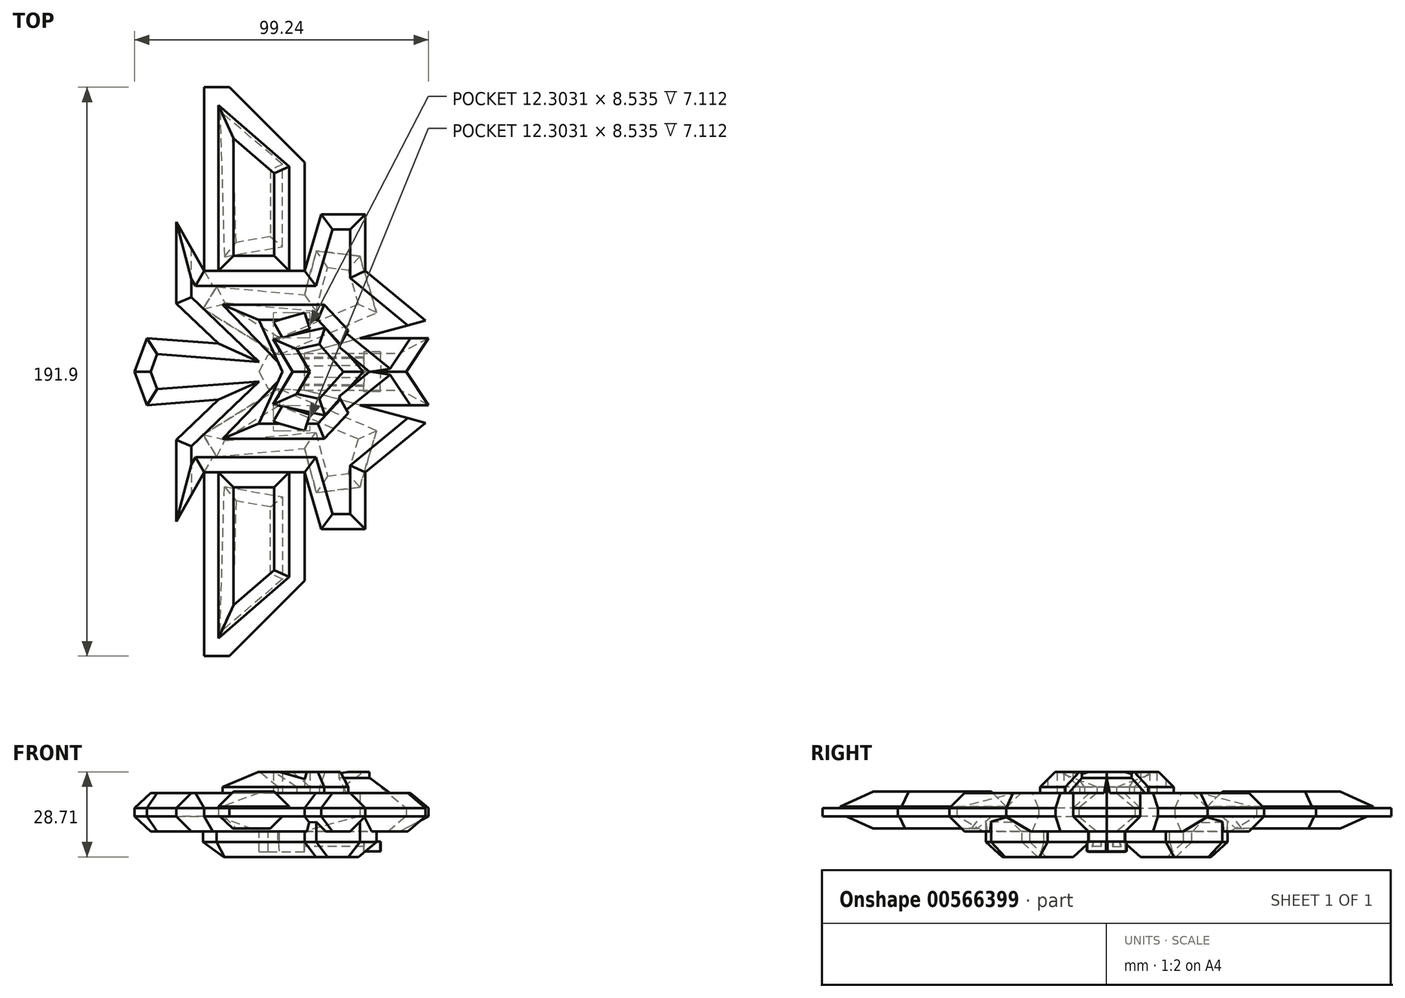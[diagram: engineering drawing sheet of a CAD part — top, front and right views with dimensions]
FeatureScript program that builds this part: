
annotation { "Feature Type Name" : "Feature", "Feature Type Description" : "" }
export const myFeature = defineFeature(function(context is Context, id is Id, definition is map)
    precondition{}
    {
        {
            var Q0;
            Q0=qCreatedBy(makeId("Top.planeOp"),FACE);
            var sketch = newSketch(context, id + "F0", { "sketchPlane" : qUnion([Q0])});
            skLineSegment(sketch, "E0", {"start": v(-57.4, 0) * mm, "end": v(-53.2, 11.26) * mm});
            skLineSegment(sketch, "E1", {"start": v(-53.2, 11.26) * mm, "end": v(-29.1, 9.47) * mm});
            skLineSegment(sketch, "E2", {"start": v(-29.1, 9.47) * mm, "end": v(-43.24, 23.02) * mm});
            skLineSegment(sketch, "E3", {"start": v(-43.24, 23.02) * mm, "end": v(-43.24, 50.52) * mm});
            skLineSegment(sketch, "E4", {"start": v(-43.24, 50.52) * mm, "end": v(-33.88, 33.98) * mm});
            skLineSegment(sketch, "E5", {"start": v(-33.88, 33.98) * mm, "end": v(0, 33.98) * mm});
            skLineSegment(sketch, "E6", {"start": v(0, 33.98) * mm, "end": v(5.58, 53.1) * mm});
            skLineSegment(sketch, "E7", {"start": v(5.58, 53.1) * mm, "end": v(20.53, 53.1) * mm});
            skLineSegment(sketch, "E8", {"start": v(20.53, 53.1) * mm, "end": v(20.53, 33.98) * mm});
            skLineSegment(sketch, "E9", {"start": v(20.53, 33.98) * mm, "end": v(40.85, 17.24) * mm});
            skLineSegment(sketch, "E10", {"start": v(40.85, 17.24) * mm, "end": v(18.73, 11.26) * mm});
            skLineSegment(sketch, "E11", {"start": v(18.73, 11.26) * mm, "end": v(41.85, 11.26) * mm});
            skLineSegment(sketch, "E12", {"start": v(41.85, 11.26) * mm, "end": v(34.28, 0) * mm});
            skLineSegment(sketch, "E13", {"start": v(34.28, 0) * mm, "end": v(-57.4, 0) * mm});
            skSolve(sketch);
        }
        {
            var Q0;
            Q0 = qSketchRegion(id + "F0", true);
            extrude(context, id + "F1", {"entities" : qUnion([Q0]), "depth" : 12.95 * mm, "offsetDistance" : 25.4 * mm});
        }
        {
            var Q0;
            Q0=makeQuery(id+"F1.opExtrude","CAP_EDGE",EDGE,{"disambiguationData":[OSD([sQuery(id+"F0.wireOp",EDGE,"E0")])],"isStart":false});
            var Q1;
            Q1=makeQuery(id+"F1.opExtrude","CAP_EDGE",EDGE,{"disambiguationData":[OSD([sQuery(id+"F0.wireOp",EDGE,"E2")])],"isStart":false});
            var Q2;
            Q2=makeQuery(id+"F1.opExtrude","CAP_EDGE",EDGE,{"disambiguationData":[OSD([sQuery(id+"F0.wireOp",EDGE,"E3")])],"isStart":false});
            var Q3;
            Q3=makeQuery(id+"F1.opExtrude","CAP_EDGE",EDGE,{"disambiguationData":[OSD([sQuery(id+"F0.wireOp",EDGE,"E1")])],"isStart":false});
            var Q4;
            Q4=makeQuery(id+"F1.opExtrude","CAP_EDGE",EDGE,{"disambiguationData":[OSD([sQuery(id+"F0.wireOp",EDGE,"E4")])],"isStart":false});
            var Q5;
            Q5=makeQuery(id+"F1.opExtrude","CAP_EDGE",EDGE,{"disambiguationData":[OSD([sQuery(id+"F0.wireOp",EDGE,"E5")])],"isStart":false});
            var Q6;
            Q6=makeQuery(id+"F1.opExtrude","CAP_EDGE",EDGE,{"disambiguationData":[OSD([sQuery(id+"F0.wireOp",EDGE,"E6")])],"isStart":false});
            var Q7;
            Q7=makeQuery(id+"F1.opExtrude","CAP_EDGE",EDGE,{"disambiguationData":[OSD([sQuery(id+"F0.wireOp",EDGE,"E8")])],"isStart":false});
            var Q8;
            Q8=makeQuery(id+"F1.opExtrude","CAP_EDGE",EDGE,{"disambiguationData":[OSD([sQuery(id+"F0.wireOp",EDGE,"E7")])],"isStart":false});
            var Q9;
            Q9=makeQuery(id+"F1.opExtrude","CAP_EDGE",EDGE,{"disambiguationData":[OSD([sQuery(id+"F0.wireOp",EDGE,"E9")])],"isStart":false});
            var Q10;
            Q10=makeQuery(id+"F1.opExtrude","CAP_EDGE",EDGE,{"disambiguationData":[OSD([sQuery(id+"F0.wireOp",EDGE,"E11")])],"isStart":true});
            var Q11;
            Q11=makeQuery(id+"F1.opExtrude","CAP_EDGE",EDGE,{"disambiguationData":[OSD([sQuery(id+"F0.wireOp",EDGE,"E12")])],"isStart":false});
            chamfer(context, id + "F2", {"entities" : qUnion([Q0, Q1, Q2, Q3, Q4, Q5, Q6, Q7, Q8, Q9, Q10, Q11]), "width" : 5.08 * mm, "tangentPropagation" : true});
        }
        {
            var Q0;
            Q0=makeQuery(id+"F1.opExtrude","CAP_FACE",FACE,{"disambiguationData":[OSD([sQuery(id+"F0.wireOp",EDGE,"E0"),sQuery(id+"F0.wireOp",EDGE,"E1"),sQuery(id+"F0.wireOp",EDGE,"E2"),sQuery(id+"F0.wireOp",EDGE,"E3"),sQuery(id+"F0.wireOp",EDGE,"E4"),sQuery(id+"F0.wireOp",EDGE,"E5"),sQuery(id+"F0.wireOp",EDGE,"E6"),sQuery(id+"F0.wireOp",EDGE,"E7"),sQuery(id+"F0.wireOp",EDGE,"E8"),sQuery(id+"F0.wireOp",EDGE,"E9"),sQuery(id+"F0.wireOp",EDGE,"E10"),sQuery(id+"F0.wireOp",EDGE,"E11"),sQuery(id+"F0.wireOp",EDGE,"E12"),sQuery(id+"F0.wireOp",EDGE,"E13")])],"isStart":false});
            var sketch = newSketch(context, id + "F3", { "sketchPlane" : qUnion([Q0])});
            skLineSegment(sketch, "E14", {"start": v(-8.99, 3.35) * mm, "end": v(-27.62, 22.55) * mm});
            skLineSegment(sketch, "E15", {"start": v(-27.62, 22.55) * mm, "end": v(6.61, 22.55) * mm});
            skLineSegment(sketch, "E16", {"start": v(6.61, 22.55) * mm, "end": v(14.75, 13.94) * mm});
            skLineSegment(sketch, "E17", {"start": v(14.75, 13.94) * mm, "end": v(11.64, 8.39) * mm});
            skLineSegment(sketch, "E18", {"start": v(11.64, 8.39) * mm, "end": v(21.94, 0) * mm});
            skLineSegment(sketch, "E19", {"start": v(21.94, 0) * mm, "end": v(13.07, 0) * mm});
            skLineSegment(sketch, "E20", {"start": v(13.07, 0) * mm, "end": v(5.04, 9.2) * mm});
            skLineSegment(sketch, "E21", {"start": v(5.04, 9.2) * mm, "end": v(-2.64, 7.56) * mm});
            skLineSegment(sketch, "E22", {"start": v(-2.64, 7.56) * mm, "end": v(1.8, 0) * mm});
            skLineSegment(sketch, "E23", {"start": v(1.8, 0) * mm, "end": v(-7.47, 0) * mm});
            skLineSegment(sketch, "E24", {"start": v(-7.47, 0) * mm, "end": v(-8.99, 3.35) * mm});
            skLineSegment(sketch, "E25", {"start": v(-10.5, 16.83) * mm, "end": v(-7.47, 11.45) * mm});
            skPoint(sketch, "E25.startSnap0", {"position": v(-10.5, 22.55) * mm});
            skLineSegment(sketch, "E26", {"start": v(-7.47, 11.45) * mm, "end": v(1.8, 14.47) * mm});
            skLineSegment(sketch, "E27", {"start": v(1.8, 14.47) * mm, "end": v(0, 19.98) * mm});
            skLineSegment(sketch, "E28", {"start": v(0, 19.98) * mm, "end": v(-10.5, 16.83) * mm});
            skSolve(sketch);
        }
        {
            var Q0;
            Q0 = qSketchRegion(id + "F3", true);
            extrude(context, id + "F4", {"entities" : qUnion([Q0]), "operationType" : NewBodyOperationType.ADD, "depth" : 7.11 * mm, "offsetDistance" : 25.4 * mm});
        }
        {
            var Q0;
            Q0=makeQuery(id+"F4.opExtrude","CAP_EDGE",EDGE,{"disambiguationData":[OSD([sQuery(id+"F3.wireOp",EDGE,"E15")])],"isStart":false});
            var Q1;
            Q1=makeQuery(id+"F4.opExtrude","CAP_EDGE",EDGE,{"disambiguationData":[OSD([sQuery(id+"F3.wireOp",EDGE,"E16")])],"isStart":false});
            var Q2;
            Q2=makeQuery(id+"F4.opExtrude","CAP_EDGE",EDGE,{"disambiguationData":[OSD([sQuery(id+"F3.wireOp",EDGE,"E18")])],"isStart":true});
            var Q3;
            Q3=makeQuery(id+"F4.opExtrude","CAP_EDGE",EDGE,{"disambiguationData":[OSD([sQuery(id+"F3.wireOp",EDGE,"E14")])],"isStart":false});
            var Q4;
            Q4=makeQuery(id+"F4.opExtrude","CAP_EDGE",EDGE,{"disambiguationData":[OSD([sQuery(id+"F3.wireOp",EDGE,"E21")])],"isStart":false});
            var Q5;
            Q5=makeQuery(id+"F4.opExtrude","CAP_EDGE",EDGE,{"disambiguationData":[OSD([sQuery(id+"F3.wireOp",EDGE,"E20")])],"isStart":false});
            var Q6;
            Q6=makeQuery(id+"F4.opExtrude","CAP_EDGE",EDGE,{"disambiguationData":[OSD([sQuery(id+"F3.wireOp",EDGE,"E22")])],"isStart":false});
            chamfer(context, id + "F5", {"entities" : qUnion([Q0, Q1, Q2, Q3, Q4, Q5, Q6]), "width" : 5.08 * mm, "tangentPropagation" : true});
        }
        {
            var Q0;
            Q0=makeQuery(id+"F1.opExtrude","CAP_FACE",FACE,{"disambiguationData":[OSD([sQuery(id+"F0.wireOp",EDGE,"E0"),sQuery(id+"F0.wireOp",EDGE,"E1"),sQuery(id+"F0.wireOp",EDGE,"E2"),sQuery(id+"F0.wireOp",EDGE,"E3"),sQuery(id+"F0.wireOp",EDGE,"E4"),sQuery(id+"F0.wireOp",EDGE,"E5"),sQuery(id+"F0.wireOp",EDGE,"E6"),sQuery(id+"F0.wireOp",EDGE,"E7"),sQuery(id+"F0.wireOp",EDGE,"E8"),sQuery(id+"F0.wireOp",EDGE,"E9"),sQuery(id+"F0.wireOp",EDGE,"E10"),sQuery(id+"F0.wireOp",EDGE,"E11"),sQuery(id+"F0.wireOp",EDGE,"E12"),sQuery(id+"F0.wireOp",EDGE,"E13")])],"isStart":true});
            var sketch = newSketch(context, id + "F6", { "sketchPlane" : qUnion([Q0])});
            skLineSegment(sketch, "E29", {"start": v(24.3, -19.9) * mm, "end": v(-8.87, -5.66) * mm});
            skLineSegment(sketch, "E30", {"start": v(-8.87, -5.66) * mm, "end": v(-34.2, -21.2) * mm});
            skLineSegment(sketch, "E31", {"start": v(-34.2, -21.2) * mm, "end": v(-29.64, -28.65) * mm});
            skLineSegment(sketch, "E32", {"start": v(-29.64, -28.65) * mm, "end": v(0, -25.9) * mm});
            skLineSegment(sketch, "E33", {"start": v(0, -25.9) * mm, "end": v(3.99, -40.8) * mm});
            skLineSegment(sketch, "E34", {"start": v(3.99, -40.8) * mm, "end": v(18.64, -38.95) * mm});
            skLineSegment(sketch, "E35", {"start": v(18.64, -38.95) * mm, "end": v(24.3, -19.9) * mm});
            skSolve(sketch);
        }
        {
            var Q0;
            Q0 = qSketchRegion(id + "F6", true);
            extrude(context, id + "F7", {"entities" : qUnion([Q0]), "operationType" : NewBodyOperationType.ADD, "depth" : 8.64 * mm, "offsetDistance" : 25.4 * mm});
        }
        {
            var Q0;
            Q0=makeQuery(id+"F7.opExtrude","CAP_EDGE",EDGE,{"disambiguationData":[OSD([sQuery(id+"F6.wireOp",EDGE,"E35")])],"isStart":false});
            var Q1;
            Q1=makeQuery(id+"F7.opExtrude","CAP_EDGE",EDGE,{"disambiguationData":[OSD([sQuery(id+"F6.wireOp",EDGE,"E33")])],"isStart":false});
            var Q2;
            Q2=makeQuery(id+"F7.opExtrude","CAP_EDGE",EDGE,{"disambiguationData":[OSD([sQuery(id+"F6.wireOp",EDGE,"E29")])],"isStart":false});
            var Q3;
            Q3=makeQuery(id+"F7.opExtrude","CAP_EDGE",EDGE,{"disambiguationData":[OSD([sQuery(id+"F6.wireOp",EDGE,"E30")])],"isStart":false});
            var Q4;
            Q4=makeQuery(id+"F7.opExtrude","CAP_EDGE",EDGE,{"disambiguationData":[OSD([sQuery(id+"F6.wireOp",EDGE,"E31")])],"isStart":false});
            var Q5;
            Q5=makeQuery(id+"F7.opExtrude","CAP_EDGE",EDGE,{"disambiguationData":[OSD([sQuery(id+"F6.wireOp",EDGE,"E32")])],"isStart":false});
            var Q6;
            Q6=makeQuery(id+"F7.opExtrude","CAP_EDGE",EDGE,{"disambiguationData":[OSD([sQuery(id+"F6.wireOp",EDGE,"E34")])],"isStart":false});
            chamfer(context, id + "F8", {"entities" : qUnion([Q0, Q1, Q2, Q3, Q4, Q5, Q6]), "width" : 5.08 * mm, "tangentPropagation" : true});
        }
        {
            var Q0;
            Q0=makeQuery(id+"F1.opExtrude","CAP_EDGE",EDGE,{"disambiguationData":[OSD([sQuery(id+"F0.wireOp",EDGE,"E0")])],"isStart":true});
            var Q1;
            Q1=makeQuery(id+"F1.opExtrude","CAP_EDGE",EDGE,{"disambiguationData":[OSD([sQuery(id+"F0.wireOp",EDGE,"E1")])],"isStart":true});
            var Q2;
            Q2=makeQuery(id+"F1.opExtrude","CAP_EDGE",EDGE,{"disambiguationData":[OSD([sQuery(id+"F0.wireOp",EDGE,"E2")])],"isStart":true});
            var Q3;
            Q3=makeQuery(id+"F1.opExtrude","CAP_EDGE",EDGE,{"disambiguationData":[OSD([sQuery(id+"F0.wireOp",EDGE,"E3")])],"isStart":true});
            var Q4;
            Q4=makeQuery(id+"F1.opExtrude","CAP_EDGE",EDGE,{"disambiguationData":[OSD([sQuery(id+"F0.wireOp",EDGE,"E5")])],"isStart":true});
            var Q5;
            Q5=makeQuery(id+"F1.opExtrude","CAP_EDGE",EDGE,{"disambiguationData":[OSD([sQuery(id+"F0.wireOp",EDGE,"E6")])],"isStart":true});
            var Q6;
            Q6=makeQuery(id+"F1.opExtrude","CAP_EDGE",EDGE,{"disambiguationData":[OSD([sQuery(id+"F0.wireOp",EDGE,"E7")])],"isStart":true});
            var Q7;
            Q7=makeQuery(id+"F1.opExtrude","CAP_EDGE",EDGE,{"disambiguationData":[OSD([sQuery(id+"F0.wireOp",EDGE,"E8")])],"isStart":true});
            var Q8;
            Q8=makeQuery(id+"F1.opExtrude","CAP_EDGE",EDGE,{"disambiguationData":[OSD([sQuery(id+"F0.wireOp",EDGE,"E9")])],"isStart":true});
            var Q9;
            Q9=makeQuery(id+"F1.opExtrude","CAP_EDGE",EDGE,{"disambiguationData":[OSD([sQuery(id+"F0.wireOp",EDGE,"E12")])],"isStart":true});
            chamfer(context, id + "F9", {"entities" : qUnion([Q0, Q1, Q2, Q3, Q4, Q5, Q6, Q7, Q8, Q9]), "width" : 5.08 * mm, "tangentPropagation" : true});
        }
        {
            var Q0;
            Q0=makeQuery(id+"F1.opExtrude","SWEPT_FACE",FACE,{"disambiguationData":[OSD([sQuery(id+"F0.wireOp",EDGE,"E5")])]});
            var sketch = newSketch(context, id + "F10", { "sketchPlane" : qUnion([Q0])});
            skLineSegment(sketch, "E36", {"start": v(33.88, 7.87) * mm, "end": v(33.88, 5.08) * mm});
            skLineSegment(sketch, "E37", {"start": v(33.88, 5.08) * mm, "end": v(0, 5.08) * mm});
            skLineSegment(sketch, "E38", {"start": v(0, 5.08) * mm, "end": v(0, 7.87) * mm});
            skLineSegment(sketch, "E39", {"start": v(0, 7.87) * mm, "end": v(33.88, 7.87) * mm});
            skSolve(sketch);
        }
        {
            var Q0;
            Q0 = qSketchRegion(id + "F10", true);
            extrude(context, id + "F11", {"entities" : qUnion([Q0]), "operationType" : NewBodyOperationType.ADD, "depth" : 61.98 * mm, "offsetDistance" : 25.4 * mm});
        }
        {
            var Q0;
            Q0=makeQuery(id+"F11.opExtrude","CAP_EDGE",EDGE,{"disambiguationData":[OSD([sQuery(id+"F10.wireOp",EDGE,"E38")])],"isStart":false});
            chamfer(context, id + "F12", {"entities" : qUnion([Q0]), "width" : 25.4 * mm, "tangentPropagation" : true});
        }
        {
            var Q0;
            Q0=makeQuery(id+"F11.opExtrude","SWEPT_FACE",FACE,{"disambiguationData":[OSD([sQuery(id+"F10.wireOp",EDGE,"E39")])]});
            var sketch = newSketch(context, id + "F13", { "sketchPlane" : qUnion([Q0])});
            skLineSegment(sketch, "E40", {"start": v(-29.04, 33.98) * mm, "end": v(-29.04, 89.9) * mm});
            skLineSegment(sketch, "E41", {"start": v(-29.04, 89.9) * mm, "end": v(-5.18, 69.2) * mm});
            skLineSegment(sketch, "E42", {"start": v(-5.18, 69.2) * mm, "end": v(-5.18, 33.98) * mm});
            skLineSegment(sketch, "E43", {"start": v(-5.18, 33.98) * mm, "end": v(-29.04, 33.98) * mm});
            skSolve(sketch);
        }
        {
            var Q0;
            Q0 = qSketchRegion(id + "F13", true);
            extrude(context, id + "F14", {"entities" : qUnion([Q0]), "operationType" : NewBodyOperationType.ADD, "depth" : 5.6 * mm, "offsetDistance" : 25.4 * mm});
        }
        {
            var Q0;
            Q0=makeQuery(id+"F14.opExtrude","CAP_EDGE",EDGE,{"disambiguationData":[OSD([sQuery(id+"F13.wireOp",EDGE,"E40")])],"isStart":false});
            var Q1;
            Q1=makeQuery(id+"F14.opExtrude","CAP_EDGE",EDGE,{"disambiguationData":[OSD([sQuery(id+"F13.wireOp",EDGE,"E41")])],"isStart":false});
            var Q2;
            Q2=makeQuery(id+"F14.opExtrude","CAP_EDGE",EDGE,{"disambiguationData":[OSD([sQuery(id+"F13.wireOp",EDGE,"E42")])],"isStart":false});
            var Q3;
            Q3=makeQuery(id+"F14.opExtrude","CAP_EDGE",EDGE,{"disambiguationData":[OSD([sQuery(id+"F13.wireOp",EDGE,"E43")])],"isStart":false});
            chamfer(context, id + "F15", {"entities" : qUnion([Q0, Q1, Q2, Q3]), "width" : 5.08 * mm, "tangentPropagation" : true});
        }
        {
            var Q0;
            Q0=makeQuery(id+"F11.opExtrude","SWEPT_FACE",FACE,{"disambiguationData":[OSD([sQuery(id+"F10.wireOp",EDGE,"E37")])]});
            var sketch = newSketch(context, id + "F16", { "sketchPlane" : qUnion([Q0])});
            skLineSegment(sketch, "E44", {"start": v(-29.59, -90.15) * mm, "end": v(-6.43, -70.44) * mm});
            skLineSegment(sketch, "E45", {"start": v(-6.43, -70.44) * mm, "end": v(-6.43, -41.3) * mm});
            skLineSegment(sketch, "E46", {"start": v(-6.43, -41.3) * mm, "end": v(-28.05, -37.59) * mm});
            skLineSegment(sketch, "E47", {"start": v(-28.05, -37.59) * mm, "end": v(-29.59, -90.15) * mm});
            skSolve(sketch);
        }
        {
            var Q0;
            Q0 = qSketchRegion(id + "F16", true);
            extrude(context, id + "F17", {"entities" : qUnion([Q0]), "operationType" : NewBodyOperationType.ADD, "depth" : 4.06 * mm, "offsetDistance" : 25.4 * mm});
        }
        {
            var Q0;
            Q0=makeQuery(id+"F17.opExtrude","CAP_EDGE",EDGE,{"disambiguationData":[OSD([sQuery(id+"F16.wireOp",EDGE,"E47")])],"isStart":false});
            var Q1;
            Q1=makeQuery(id+"F17.opExtrude","CAP_EDGE",EDGE,{"disambiguationData":[OSD([sQuery(id+"F16.wireOp",EDGE,"E44")])],"isStart":false});
            var Q2;
            Q2=makeQuery(id+"F17.opExtrude","CAP_FACE",FACE,{"disambiguationData":[OSD([sQuery(id+"F16.wireOp",EDGE,"E44"),sQuery(id+"F16.wireOp",EDGE,"E45"),sQuery(id+"F16.wireOp",EDGE,"E46"),sQuery(id+"F16.wireOp",EDGE,"E47")])],"isStart":false});
            chamfer(context, id + "F18", {"entities" : qUnion([Q0, Q1, Q2]), "width" : 5.08 * mm, "tangentPropagation" : true});
        }
        {
            var Q0;
            Q0=makeQuery(id+"F1.opExtrude","SWEPT_BODY",BODY,{"disambiguationData":[OSD([sQuery(id+"F0.wireOp",EDGE,"E0"),sQuery(id+"F0.wireOp",EDGE,"E1"),sQuery(id+"F0.wireOp",EDGE,"E2"),sQuery(id+"F0.wireOp",EDGE,"E3"),sQuery(id+"F0.wireOp",EDGE,"E4"),sQuery(id+"F0.wireOp",EDGE,"E5"),sQuery(id+"F0.wireOp",EDGE,"E6"),sQuery(id+"F0.wireOp",EDGE,"E7"),sQuery(id+"F0.wireOp",EDGE,"E8"),sQuery(id+"F0.wireOp",EDGE,"E9"),sQuery(id+"F0.wireOp",EDGE,"E10"),sQuery(id+"F0.wireOp",EDGE,"E11"),sQuery(id+"F0.wireOp",EDGE,"E12"),sQuery(id+"F0.wireOp",EDGE,"E13")])]});
            var Q1;
            Q1=qCreatedBy(makeId("Front.planeOp"),FACE);
            mirror(context, id + "F19", {"operationType" : NewBodyOperationType.ADD, "entities" : qUnion([Q0]), "mirrorPlane" : qUnion([Q1])});
        }
        {
            var Q0;
            {var subQ0=makeQuery(id+"F9.opChamfer","SPLIT",FACE,{"disambiguationData":[OD(1.0)],"derivedFrom":makeQuery(id+"F1.opExtrude","CAP_FACE",FACE,{"disambiguationData":[OSD([sQuery(id+"F0.wireOp",EDGE,"E0"),sQuery(id+"F0.wireOp",EDGE,"E1"),sQuery(id+"F0.wireOp",EDGE,"E2"),sQuery(id+"F0.wireOp",EDGE,"E3"),sQuery(id+"F0.wireOp",EDGE,"E4"),sQuery(id+"F0.wireOp",EDGE,"E5"),sQuery(id+"F0.wireOp",EDGE,"E6"),sQuery(id+"F0.wireOp",EDGE,"E7"),sQuery(id+"F0.wireOp",EDGE,"E8"),sQuery(id+"F0.wireOp",EDGE,"E9"),sQuery(id+"F0.wireOp",EDGE,"E10"),sQuery(id+"F0.wireOp",EDGE,"E11"),sQuery(id+"F0.wireOp",EDGE,"E12"),sQuery(id+"F0.wireOp",EDGE,"E13")])],"isStart":true})});Q0=makeQuery(id+"F19.boolean.opBoolean","MERGE",FACE,{"derivedFrom":[subQ0,makeQuery(id+"F19.opPattern","COPY",FACE,{"derivedFrom":subQ0,"instanceName":"1"})]});}
            var sketch = newSketch(context, id + "F20", { "sketchPlane" : qUnion([Q0])});
            skLineSegment(sketch, "E48", {"start": v(-15.37, 0) * mm, "end": v(-12.3, 5.66) * mm});
            skLineSegment(sketch, "E49", {"start": v(-12.3, 5.66) * mm, "end": v(-0.06, 6.18) * mm});
            skLineSegment(sketch, "E50", {"start": v(-0.06, 6.18) * mm, "end": v(0, 0) * mm});
            skLineSegment(sketch, "E51", {"start": v(0, 0) * mm, "end": v(-15.37, 0) * mm});
            skSolve(sketch);
        }
        {
            var Q0;
            Q0 = qSketchRegion(id + "F20", true);
            extrude(context, id + "F21", {"entities" : qUnion([Q0]), "operationType" : NewBodyOperationType.ADD, "depth" : 6.86 * mm, "offsetDistance" : 25.4 * mm});
        }
        {
            var Q0;
            Q0=makeQuery(id+"F21.opExtrude","SWEPT_FACE",FACE,{"disambiguationData":[OSD([sQuery(id+"F20.wireOp",EDGE,"E50")])]});
            var sketch = newSketch(context, id + "F22", { "sketchPlane" : qUnion([Q0])});
            skLineSegment(sketch, "E52", {"start": v(-4.31, -3.43) * mm, "end": v(-1.89, -3.43) * mm});
            skPoint(sketch, "E52.startSnap0", {"position": v(-6.18, -3.43) * mm});
            skPoint(sketch, "E52.endSnap0", {"position": v(0, -3.43) * mm});
            skLineSegment(sketch, "E53", {"start": v(-1.89, -3.43) * mm, "end": v(-1.89, -5.18) * mm});
            skLineSegment(sketch, "E54", {"start": v(-1.89, -5.18) * mm, "end": v(-4.73, -5.18) * mm});
            skLineSegment(sketch, "E55", {"start": v(-4.73, -5.18) * mm, "end": v(-4.31, -3.43) * mm});
            skSolve(sketch);
        }
        {
            var Q0;
            Q0 = qSketchRegion(id + "F22", true);
            extrude(context, id + "F23", {"entities" : qUnion([Q0]), "operationType" : NewBodyOperationType.ADD, "depth" : 20.07 * mm, "offsetDistance" : 25.4 * mm});
        }
        {
            var Q0;
            Q0=makeQuery(id+"F23.opExtrude","CAP_FACE",FACE,{"disambiguationData":[OSD([sQuery(id+"F22.wireOp",EDGE,"E52"),sQuery(id+"F22.wireOp",EDGE,"E53"),sQuery(id+"F22.wireOp",EDGE,"E54"),sQuery(id+"F22.wireOp",EDGE,"E55")])],"isStart":false});
            var sketch = newSketch(context, id + "F24", { "sketchPlane" : qUnion([Q0])});
            skLineSegment(sketch, "E56.bottom", {"start": v(-6.5, -6.8) * mm, "end": v(0, -6.8) * mm});
            skLineSegment(sketch, "E56.top", {"start": v(-6.5, -3.43) * mm, "end": v(0, -3.43) * mm});
            skLineSegment(sketch, "E56.left", {"start": v(-6.5, -6.8) * mm, "end": v(-6.5, -3.43) * mm});
            skLineSegment(sketch, "E56.right", {"start": v(0, -6.8) * mm, "end": v(0, -3.43) * mm});
            skSolve(sketch);
        }
        {
            var Q0;
            Q0 = qSketchRegion(id + "F24", true);
            extrude(context, id + "F25", {"entities" : qUnion([Q0]), "operationType" : NewBodyOperationType.ADD, "depth" : 5.6 * mm, "offsetDistance" : 25.4 * mm});
        }
        {
            var Q0;
            Q0=makeQuery(id+"F1.opExtrude","SWEPT_BODY",BODY,{"disambiguationData":[OSD([sQuery(id+"F0.wireOp",EDGE,"E0"),sQuery(id+"F0.wireOp",EDGE,"E1"),sQuery(id+"F0.wireOp",EDGE,"E2"),sQuery(id+"F0.wireOp",EDGE,"E3"),sQuery(id+"F0.wireOp",EDGE,"E4"),sQuery(id+"F0.wireOp",EDGE,"E5"),sQuery(id+"F0.wireOp",EDGE,"E6"),sQuery(id+"F0.wireOp",EDGE,"E7"),sQuery(id+"F0.wireOp",EDGE,"E8"),sQuery(id+"F0.wireOp",EDGE,"E9"),sQuery(id+"F0.wireOp",EDGE,"E10"),sQuery(id+"F0.wireOp",EDGE,"E11"),sQuery(id+"F0.wireOp",EDGE,"E12"),sQuery(id+"F0.wireOp",EDGE,"E13")])]});
            var Q1;
            Q1=qCreatedBy(makeId("Front.planeOp"),FACE);
            mirror(context, id + "F26", {"operationType" : NewBodyOperationType.ADD, "entities" : qUnion([Q0]), "mirrorPlane" : qUnion([Q1])});
        }
    });
